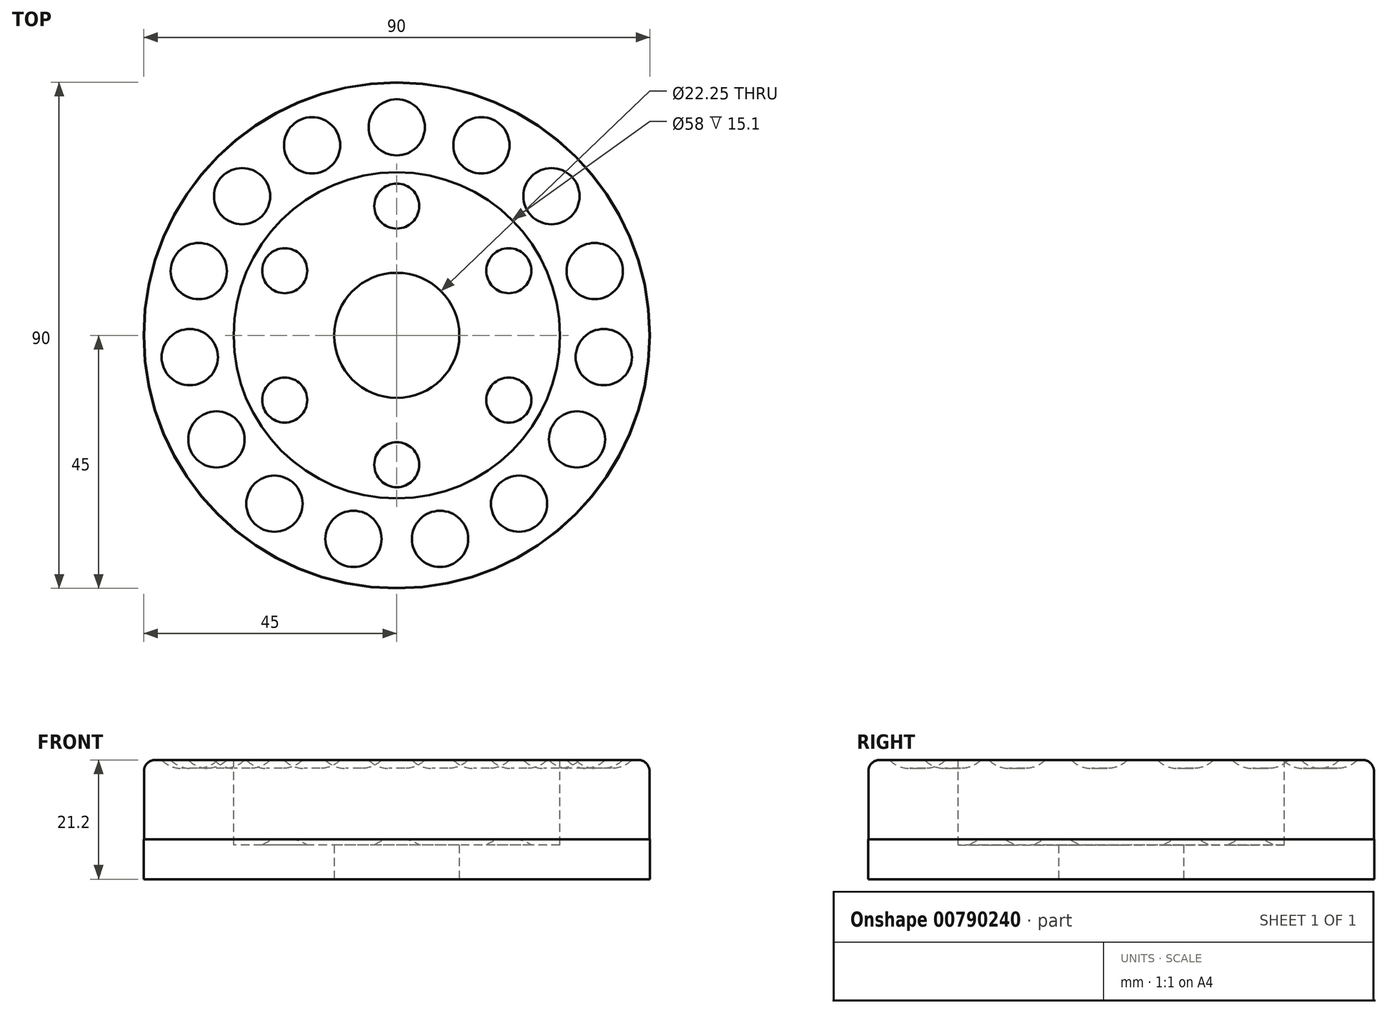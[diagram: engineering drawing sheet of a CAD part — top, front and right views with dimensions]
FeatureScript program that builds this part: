
annotation { "Feature Type Name" : "Feature", "Feature Type Description" : "" }
export const myFeature = defineFeature(function(context is Context, id is Id, definition is map)
    precondition{}
    {
        {
            var Q0;
            Q0=qCreatedBy(makeId("Top.planeOp"),FACE);
            var sketch = newSketch(context, id + "F0", { "sketchPlane" : qUnion([Q0])});
            skCircle(sketch, "E0", {"center": v(0, 0) * mm, "radius": 45 * mm});
            skCircle(sketch, "E1", {"center": v(0, 0) * mm, "radius": 11.12 * mm});
            skSolve(sketch);
        }
        {
            var Q0;
            Q0=qSketchRegion(id+"F0",true);
            extrude(context, id + "F1", {"entities" : qUnion([Q0]), "depth" : 7.1 * mm, "offsetDistance" : 25 * mm});
        }
        {
            var Q0;
            Q0=makeQuery(id+"F1.opExtrude","CAP_FACE",FACE,{"disambiguationData":[OSD([sQuery(id+"F0.wireOp",EDGE,"E0"),sQuery(id+"F0.wireOp",EDGE,"E1")])],"isStart":false});
            var sketch = newSketch(context, id + "F2", { "sketchPlane" : qUnion([Q0])});
            skCircle(sketch, "E2", {"center": v(0, 0) * mm, "radius": 44.94 * mm});
            skSolve(sketch);
        }
        {
            var Q0;
            Q0=qSketchRegion(id+"F2",true);
            extrude(context, id + "F3", {"entities" : qUnion([Q0]), "operationType" : NewBodyOperationType.ADD, "depth" : 14.1 * mm, "offsetDistance" : 25 * mm});
        }
        {
            var Q0;
            Q0=makeQuery(id+"F3.opExtrude","CAP_FACE",FACE,{"disambiguationData":[OSD([sQuery(id+"F2.wireOp",EDGE,"E2")])],"isStart":false});
            var sketch = newSketch(context, id + "F4", { "sketchPlane" : qUnion([Q0])});
            skCircle(sketch, "E3", {"center": v(0, 0) * mm, "radius": 29 * mm});
            skSolve(sketch);
        }
        {
            var Q0;
            Q0=qSketchRegion(id+"F4",true);
            extrude(context, id + "F5", {"entities" : qUnion([Q0]), "operationType" : NewBodyOperationType.REMOVE, "oppositeDirection" : true, "depth" : 15.1 * mm, "offsetDistance" : 25 * mm});
        }
        {
            var Q0;
            Q0=makeQuery(id+"F3.opExtrude","CAP_EDGE",EDGE,{"disambiguationData":[OSD([sQuery(id+"F2.wireOp",EDGE,"E2")])],"isStart":false});
            var Q1;
            Q1=makeQuery(id+"F5.boolean.opBoolean","COPY",EDGE,{"derivedFrom":makeQuery(id+"F5.opExtrude","CAP_EDGE",EDGE,{"disambiguationData":[OSD([sQuery(id+"F4.wireOp",EDGE,"E3")])],"isStart":true})});
            fillet(context, id + "F6", {"entities" : qUnion([Q0, Q1]), "radius" : 2 * mm, "tangentPropagation" : true, "allowEdgeOverflow" : false});
        }
        {
            var Q0;
            Q0=makeQuery(id+"F3.opExtrude","CAP_FACE",FACE,{"disambiguationData":[OSD([sQuery(id+"F2.wireOp",EDGE,"E2")])],"isStart":false});
            var sketch = newSketch(context, id + "F7", { "sketchPlane" : qUnion([Q0])});
            skCircle(sketch, "E4", {"center": v(0, 37) * mm, "radius": 5 * mm});
            skCircle(sketch, "E5.1.0", {"center": v(-15.05, 33.8) * mm, "radius": 5 * mm});
            skCircle(sketch, "E5.2.0", {"center": v(-27.5, 24.76) * mm, "radius": 5 * mm});
            skCircle(sketch, "E5.3.0", {"center": v(-35.19, 11.43) * mm, "radius": 5 * mm});
            skCircle(sketch, "E5.4.0", {"center": v(-36.8, -3.87) * mm, "radius": 5 * mm});
            skCircle(sketch, "E5.5.0", {"center": v(-32.04, -18.5) * mm, "radius": 5 * mm});
            skCircle(sketch, "E5.6.0", {"center": v(-21.75, -29.93) * mm, "radius": 5 * mm});
            skCircle(sketch, "E5.7.0", {"center": v(-7.7, -36.2) * mm, "radius": 5 * mm});
            skCircle(sketch, "E5.8.0", {"center": v(7.7, -36.2) * mm, "radius": 5 * mm});
            skCircle(sketch, "E5.9.0", {"center": v(21.75, -29.93) * mm, "radius": 5 * mm});
            skCircle(sketch, "E5.10.0", {"center": v(32.04, -18.5) * mm, "radius": 5 * mm});
            skCircle(sketch, "E5.11.0", {"center": v(36.8, -3.87) * mm, "radius": 5 * mm});
            skCircle(sketch, "E5.12.0", {"center": v(35.19, 11.43) * mm, "radius": 5 * mm});
            skCircle(sketch, "E5.13.0", {"center": v(27.5, 24.76) * mm, "radius": 5 * mm});
            skCircle(sketch, "E5.14.0", {"center": v(15.05, 33.8) * mm, "radius": 5 * mm});
            skPoint(sketch, "E5.center", {"position": v(0, 0) * mm});
            skSolve(sketch);
        }
        {
            var Q0;
            Q0=qSketchRegion(id+"F7",true);
            extrude(context, id + "F8", {"entities" : qUnion([Q0]), "operationType" : NewBodyOperationType.REMOVE, "oppositeDirection" : true, "depth" : 1.5 * mm, "offsetDistance" : 25 * mm});
        }
        {
            var Q0;
            Q0=makeQuery(id+"F8.boolean.opBoolean","COPY",FACE,{"derivedFrom":makeQuery(id+"F8.opExtrude","CAP_FACE",FACE,{"disambiguationData":[OSD([sQuery(id+"F7.wireOp",EDGE,"E4")])],"isStart":false})});
            var Q1;
            Q1=makeQuery(id+"F8.boolean.opBoolean","COPY",FACE,{"derivedFrom":makeQuery(id+"F8.opExtrude","CAP_FACE",FACE,{"disambiguationData":[OSD([sQuery(id+"F7.wireOp",EDGE,"E5.1.0")])],"isStart":false})});
            var Q2;
            Q2=makeQuery(id+"F8.boolean.opBoolean","COPY",FACE,{"derivedFrom":makeQuery(id+"F8.opExtrude","CAP_FACE",FACE,{"disambiguationData":[OSD([sQuery(id+"F7.wireOp",EDGE,"E5.2.0")])],"isStart":false})});
            var Q3;
            Q3=makeQuery(id+"F8.boolean.opBoolean","COPY",FACE,{"derivedFrom":makeQuery(id+"F8.opExtrude","CAP_FACE",FACE,{"disambiguationData":[OSD([sQuery(id+"F7.wireOp",EDGE,"E5.3.0")])],"isStart":false})});
            var Q4;
            Q4=makeQuery(id+"F8.boolean.opBoolean","COPY",FACE,{"derivedFrom":makeQuery(id+"F8.opExtrude","CAP_FACE",FACE,{"disambiguationData":[OSD([sQuery(id+"F7.wireOp",EDGE,"E5.4.0")])],"isStart":false})});
            var Q5;
            Q5=makeQuery(id+"F8.boolean.opBoolean","COPY",FACE,{"derivedFrom":makeQuery(id+"F8.opExtrude","CAP_FACE",FACE,{"disambiguationData":[OSD([sQuery(id+"F7.wireOp",EDGE,"E5.5.0")])],"isStart":false})});
            var Q6;
            Q6=makeQuery(id+"F8.boolean.opBoolean","COPY",FACE,{"derivedFrom":makeQuery(id+"F8.opExtrude","CAP_FACE",FACE,{"disambiguationData":[OSD([sQuery(id+"F7.wireOp",EDGE,"E5.6.0")])],"isStart":false})});
            var Q7;
            Q7=makeQuery(id+"F8.boolean.opBoolean","COPY",FACE,{"derivedFrom":makeQuery(id+"F8.opExtrude","CAP_FACE",FACE,{"disambiguationData":[OSD([sQuery(id+"F7.wireOp",EDGE,"E5.7.0")])],"isStart":false})});
            var Q8;
            Q8=makeQuery(id+"F8.boolean.opBoolean","COPY",FACE,{"derivedFrom":makeQuery(id+"F8.opExtrude","CAP_FACE",FACE,{"disambiguationData":[OSD([sQuery(id+"F7.wireOp",EDGE,"E5.8.0")])],"isStart":false})});
            var Q9;
            Q9=makeQuery(id+"F8.boolean.opBoolean","COPY",FACE,{"derivedFrom":makeQuery(id+"F8.opExtrude","CAP_FACE",FACE,{"disambiguationData":[OSD([sQuery(id+"F7.wireOp",EDGE,"E5.9.0")])],"isStart":false})});
            var Q10;
            Q10=makeQuery(id+"F8.boolean.opBoolean","COPY",FACE,{"derivedFrom":makeQuery(id+"F8.opExtrude","CAP_FACE",FACE,{"disambiguationData":[OSD([sQuery(id+"F7.wireOp",EDGE,"E5.10.0")])],"isStart":false})});
            var Q11;
            Q11=makeQuery(id+"F8.boolean.opBoolean","COPY",FACE,{"derivedFrom":makeQuery(id+"F8.opExtrude","CAP_FACE",FACE,{"disambiguationData":[OSD([sQuery(id+"F7.wireOp",EDGE,"E5.11.0")])],"isStart":false})});
            var Q12;
            Q12=makeQuery(id+"F8.boolean.opBoolean","COPY",FACE,{"derivedFrom":makeQuery(id+"F8.opExtrude","CAP_FACE",FACE,{"disambiguationData":[OSD([sQuery(id+"F7.wireOp",EDGE,"E5.12.0")])],"isStart":false})});
            var Q13;
            Q13=makeQuery(id+"F8.boolean.opBoolean","COPY",FACE,{"derivedFrom":makeQuery(id+"F8.opExtrude","CAP_FACE",FACE,{"disambiguationData":[OSD([sQuery(id+"F7.wireOp",EDGE,"E5.13.0")])],"isStart":false})});
            var Q14;
            Q14=makeQuery(id+"F8.boolean.opBoolean","COPY",FACE,{"derivedFrom":makeQuery(id+"F8.opExtrude","CAP_FACE",FACE,{"disambiguationData":[OSD([sQuery(id+"F7.wireOp",EDGE,"E5.14.0")])],"isStart":false})});
            fillet(context, id + "F9", {"entities" : qUnion([Q0, Q1, Q2, Q3, Q4, Q5, Q6, Q7, Q8, Q9, Q10, Q11, Q12, Q13, Q14]), "radius" : 5 * mm, "tangentPropagation" : true, "allowEdgeOverflow" : false});
        }
        {
            var Q0;
            Q0=makeQuery(id+"F5.boolean.opBoolean","COPY",FACE,{"derivedFrom":makeQuery(id+"F5.opExtrude","CAP_FACE",FACE,{"disambiguationData":[OSD([sQuery(id+"F4.wireOp",EDGE,"E3")])],"isStart":false})});
            var sketch = newSketch(context, id + "F10", { "sketchPlane" : qUnion([Q0])});
            skCircle(sketch, "E6", {"center": v(0, 23) * mm, "radius": 4 * mm});
            skCircle(sketch, "E7.1.0", {"center": v(-19.92, 11.5) * mm, "radius": 4 * mm});
            skCircle(sketch, "E7.2.0", {"center": v(-19.92, -11.5) * mm, "radius": 4 * mm});
            skCircle(sketch, "E7.3.0", {"center": v(0, -23) * mm, "radius": 4 * mm});
            skCircle(sketch, "E7.4.0", {"center": v(19.92, -11.5) * mm, "radius": 4 * mm});
            skCircle(sketch, "E7.5.0", {"center": v(19.92, 11.5) * mm, "radius": 4 * mm});
            skPoint(sketch, "E7.center", {"position": v(0, 0) * mm});
            skSolve(sketch);
        }
        {
            var Q0;
            Q0=qSketchRegion(id+"F10",true);
            extrude(context, id + "F11", {"entities" : qUnion([Q0]), "operationType" : NewBodyOperationType.ADD, "depth" : 1 * mm, "offsetDistance" : 25 * mm});
        }
        {
            var Q0;
            Q0=makeQuery(id+"F11.opExtrude","CAP_FACE",FACE,{"disambiguationData":[OSD([sQuery(id+"F10.wireOp",EDGE,"E6")])],"isStart":false});
            var Q1;
            Q1=makeQuery(id+"F11.opExtrude","CAP_FACE",FACE,{"disambiguationData":[OSD([sQuery(id+"F10.wireOp",EDGE,"E7.1.0")])],"isStart":false});
            var Q2;
            Q2=makeQuery(id+"F11.opExtrude","CAP_FACE",FACE,{"disambiguationData":[OSD([sQuery(id+"F10.wireOp",EDGE,"E7.2.0")])],"isStart":false});
            var Q3;
            Q3=makeQuery(id+"F11.opExtrude","CAP_FACE",FACE,{"disambiguationData":[OSD([sQuery(id+"F10.wireOp",EDGE,"E7.3.0")])],"isStart":false});
            var Q4;
            Q4=makeQuery(id+"F11.opExtrude","CAP_FACE",FACE,{"disambiguationData":[OSD([sQuery(id+"F10.wireOp",EDGE,"E7.4.0")])],"isStart":false});
            var Q5;
            Q5=makeQuery(id+"F11.opExtrude","CAP_FACE",FACE,{"disambiguationData":[OSD([sQuery(id+"F10.wireOp",EDGE,"E7.5.0")])],"isStart":false});
            fillet(context, id + "F12", {"entities" : qUnion([Q0, Q1, Q2, Q3, Q4, Q5]), "radius" : 5 * mm, "tangentPropagation" : true, "allowEdgeOverflow" : false});
        }
        {
            var Q0;
            Q0=makeQuery(id+"F5.boolean.opBoolean","COPY",FACE,{"derivedFrom":makeQuery(id+"F5.opExtrude","CAP_FACE",FACE,{"disambiguationData":[OSD([sQuery(id+"F4.wireOp",EDGE,"E3")])],"isStart":false})});
            var sketch = newSketch(context, id + "F13", { "sketchPlane" : qUnion([Q0])});
            skCircle(sketch, "E8", {"center": v(0, 0) * mm, "radius": 11.12 * mm});
            skSolve(sketch);
        }
        {
            var Q0;
            Q0=qSketchRegion(id+"F13",true);
            extrude(context, id + "F14", {"entities" : qUnion([Q0]), "operationType" : NewBodyOperationType.REMOVE, "oppositeDirection" : true, "depth" : 7.1 * mm, "offsetDistance" : 25 * mm});
        }
    });
